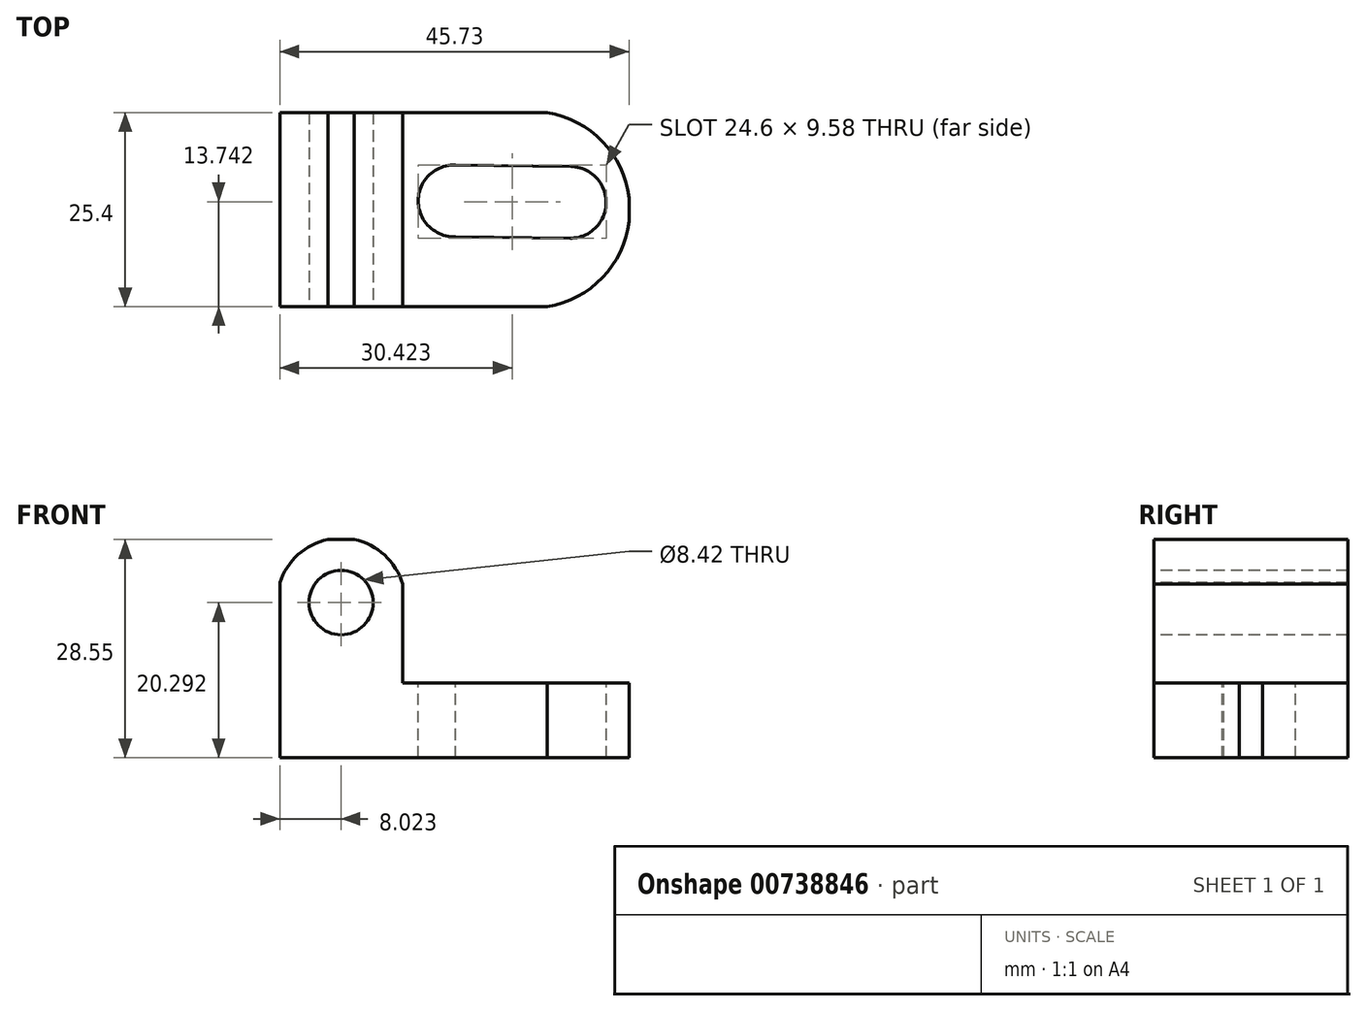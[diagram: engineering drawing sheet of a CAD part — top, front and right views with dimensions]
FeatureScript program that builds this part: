
annotation { "Feature Type Name" : "Feature", "Feature Type Description" : "" }
export const myFeature = defineFeature(function(context is Context, id is Id, definition is map)
    precondition{}
    {
        {
            var Q0;
            Q0=qCreatedBy(makeId("Front.planeOp"),FACE);
            var sketch = newSketch(context, id + "F0", { "sketchPlane" : qUnion([Q0])});
            skLineSegment(sketch, "E0", {"start": v(0, 0) * mm, "end": v(45.73, 0) * mm});
            skLineSegment(sketch, "E1", {"start": v(45.73, 0) * mm, "end": v(45.73, 9.78) * mm});
            skLineSegment(sketch, "E2", {"start": v(45.73, 9.78) * mm, "end": v(16.1, 9.78) * mm});
            skLineSegment(sketch, "E3", {"start": v(16.1, 9.78) * mm, "end": v(16.1, 28.55) * mm});
            skLineSegment(sketch, "E4", {"start": v(16.1, 28.55) * mm, "end": v(0, 28.55) * mm});
            skLineSegment(sketch, "E5", {"start": v(0, 28.55) * mm, "end": v(0, 0) * mm});
            skSolve(sketch);
        }
        {
            var Q0;
            Q0=makeQuery(id+"F0.imprint","IMPRINT",FACE,{"disambiguationData":[TD([[makeQuery(id+"F0.imprint","IMPRINT",EDGE,{"derivedFrom":sQuery(id+"F0.wireOp",EDGE,"E0")}),1.0]])]});
            extrude(context, id + "F1", {"entities" : qUnion([Q0]), "depth" : 25.4 * mm, "offsetDistance" : 25.4 * mm});
        }
        {
            var Q0;
            Q0=makeQuery(id+"F1.opExtrude","SWEPT_FACE",FACE,{"disambiguationData":[OSD([sQuery(id+"F0.wireOp",EDGE,"E2")])]});
            var sketch = newSketch(context, id + "F2", { "sketchPlane" : qUnion([Q0])});
            skCircle(sketch, "E6", {"center": v(22.82, -11.56) * mm, "radius": 4.7 * mm});
            skCircle(sketch, "E7", {"center": v(38.03, -11.75) * mm, "radius": 4.7 * mm});
            skLineSegment(sketch, "E8", {"start": v(23.01, -6.87) * mm, "end": v(38.09, -7.06) * mm});
            skLineSegment(sketch, "E9", {"start": v(23.01, -16.25) * mm, "end": v(38.03, -16.45) * mm});
            skSolve(sketch);
        }
        {
            var Q0;
            {var subQ0=sQuery(id+"F2.wireOp",EDGE,"E6");var subQ1=makeQuery(id+"F2.imprint","INTERSECT",VERTEX,{"derivedFrom":[subQ0,sQuery(id+"F2.wireOp",EDGE,"E8")]});Q0=makeQuery(id+"F2.imprint","IMPRINT",FACE,{"disambiguationData":[TD([[makeQuery(id+"F2.imprint","IMPRINT",EDGE,{"disambiguationData":[TD([[subQ1,-1.0]])],"derivedFrom":subQ0}),1.0]])]});}
            var Q1;
            {var subQ0=sQuery(id+"F2.wireOp",EDGE,"E8");Q1=makeQuery(id+"F2.imprint","IMPRINT",FACE,{"disambiguationData":[TD([[makeQuery(id+"F2.imprint","IMPRINT",EDGE,{"derivedFrom":subQ0}),-1.0]])]});}
            var Q2;
            {var subQ0=sQuery(id+"F2.wireOp",EDGE,"E7");var subQ1=makeQuery(id+"F2.imprint","INTERSECT",VERTEX,{"derivedFrom":[subQ0,sQuery(id+"F2.wireOp",EDGE,"E8")]});Q2=makeQuery(id+"F2.imprint","IMPRINT",FACE,{"disambiguationData":[TD([[makeQuery(id+"F2.imprint","IMPRINT",EDGE,{"disambiguationData":[TD([[subQ1,-1.0]])],"derivedFrom":subQ0}),1.0]])]});}
            extrude(context, id + "F3", {"entities" : qUnion([Q0, Q1, Q2]), "operationType" : NewBodyOperationType.REMOVE, "endBound" : BoundingType.THROUGH_ALL, "oppositeDirection" : true, "depth" : 25.4 * mm, "offsetDistance" : 25.4 * mm});
        }
        {
            var Q0;
            Q0=makeQuery(id+"F1.opExtrude","SWEPT_FACE",FACE,{"disambiguationData":[OSD([sQuery(id+"F0.wireOp",EDGE,"E2")])]});
            var sketch = newSketch(context, id + "F4", { "sketchPlane" : qUnion([Q0])});
            skArc(sketch, "E10", {"start": v(30.92, -25.4) * mm, "mid": v(45.82, -12.7) * mm, "end": v(30.92, 0) * mm});
            skSolve(sketch);
        }
        {
            var Q0;
            {var subQ0=sQuery(id+"F4.wireOp",EDGE,"E10");var subQ1=sQuery(id+"F0.wireOp",EDGE,"E2");var subQ4=makeQuery(id+"F1.opExtrude","CAP_EDGE",EDGE,{"disambiguationData":[OSD([subQ1])],"isStart":true});var subQ5=makeQuery(id+"F4.imprint","INTERSECT",VERTEX,{"disambiguationData":[OD(1.0)],"derivedFrom":[subQ4,subQ0]});Q0=makeQuery(id+"F4.imprint","IMPRINT",FACE,{"disambiguationData":[TD([[makeQuery(id+"F4.imprint","IMPRINT",EDGE,{"disambiguationData":[TD([[subQ5,1.0]])],"derivedFrom":subQ0}),-1.0]])]});}
            var Q1;
            {var subQ0=sQuery(id+"F4.wireOp",EDGE,"E10");var subQ1=sQuery(id+"F0.wireOp",EDGE,"E2");var subQ2=makeQuery(id+"F1.opExtrude","CAP_EDGE",EDGE,{"disambiguationData":[OSD([subQ1])],"isStart":false});var subQ3=makeQuery(id+"F4.imprint","INTERSECT",VERTEX,{"disambiguationData":[OD(1.0)],"derivedFrom":[subQ2,subQ0]});Q1=makeQuery(id+"F4.imprint","IMPRINT",FACE,{"disambiguationData":[TD([[makeQuery(id+"F4.imprint","IMPRINT",EDGE,{"disambiguationData":[TD([[subQ3,-1.0]])],"derivedFrom":subQ0}),-1.0]])]});}
            extrude(context, id + "F5", {"entities" : qUnion([Q0, Q1]), "operationType" : NewBodyOperationType.REMOVE, "endBound" : BoundingType.THROUGH_ALL, "oppositeDirection" : true, "depth" : 25.4 * mm, "offsetDistance" : 25.4 * mm});
        }
        {
            var Q0;
            Q0=makeQuery(id+"F1.opExtrude","CAP_FACE",FACE,{"disambiguationData":[OSD([sQuery(id+"F0.wireOp",EDGE,"E0"),sQuery(id+"F0.wireOp",EDGE,"E1"),sQuery(id+"F0.wireOp",EDGE,"E2"),sQuery(id+"F0.wireOp",EDGE,"E3"),sQuery(id+"F0.wireOp",EDGE,"E4"),sQuery(id+"F0.wireOp",EDGE,"E5")])],"isStart":false});
            var sketch = newSketch(context, id + "F6", { "sketchPlane" : qUnion([Q0])});
            skArc(sketch, "E11", {"start": v(16.1, 17.87) * mm, "mid": v(7.93, 28.72) * mm, "end": v(0, 17.7) * mm});
            skSolve(sketch);
        }
        {
            var Q0;
            {var subQ0=sQuery(id+"F6.wireOp",EDGE,"E11");var subQ1=makeQuery(id+"F1.opExtrude","CAP_EDGE",EDGE,{"disambiguationData":[OSD([sQuery(id+"F0.wireOp",EDGE,"E4")])],"isStart":false});var subQ2=makeQuery(id+"F6.imprint","INTERSECT",VERTEX,{"disambiguationData":[OD(1.0)],"derivedFrom":[subQ1,subQ0]});Q0=makeQuery(id+"F6.imprint","IMPRINT",FACE,{"disambiguationData":[TD([[makeQuery(id+"F6.imprint","IMPRINT",EDGE,{"disambiguationData":[TD([[subQ2,-1.0]])],"derivedFrom":subQ0}),-1.0]])]});}
            var Q1;
            {var subQ0=sQuery(id+"F6.wireOp",EDGE,"E11");var subQ1=makeQuery(id+"F1.opExtrude","CAP_EDGE",EDGE,{"disambiguationData":[OSD([sQuery(id+"F0.wireOp",EDGE,"E3")])],"isStart":false});var subQ2=makeQuery(id+"F6.imprint","INTERSECT",VERTEX,{"disambiguationData":[OD(1.0)],"derivedFrom":[subQ1,subQ0]});Q1=makeQuery(id+"F6.imprint","IMPRINT",FACE,{"disambiguationData":[TD([[makeQuery(id+"F6.imprint","IMPRINT",EDGE,{"disambiguationData":[TD([[subQ2,-1.0]])],"derivedFrom":subQ0}),-1.0]])]});}
            extrude(context, id + "F7", {"entities" : qUnion([Q0, Q1]), "operationType" : NewBodyOperationType.REMOVE, "endBound" : BoundingType.THROUGH_ALL, "oppositeDirection" : true, "depth" : 25.4 * mm, "offsetDistance" : 25.4 * mm});
        }
        {
            var Q0;
            Q0=makeQuery(id+"F1.opExtrude","CAP_FACE",FACE,{"disambiguationData":[OSD([sQuery(id+"F0.wireOp",EDGE,"E0"),sQuery(id+"F0.wireOp",EDGE,"E1"),sQuery(id+"F0.wireOp",EDGE,"E2"),sQuery(id+"F0.wireOp",EDGE,"E3"),sQuery(id+"F0.wireOp",EDGE,"E4"),sQuery(id+"F0.wireOp",EDGE,"E5")])],"isStart":false});
            var sketch = newSketch(context, id + "F8", { "sketchPlane" : qUnion([Q0])});
            skCircle(sketch, "E12", {"center": v(8.02, 20.3) * mm, "radius": 4.2 * mm});
            skSolve(sketch);
        }
        {
            var Q0;
            Q0=makeQuery(id+"F8.imprint","IMPRINT",FACE,{"disambiguationData":[TD([[makeQuery(id+"F8.imprint","IMPRINT",EDGE,{"derivedFrom":sQuery(id+"F8.wireOp",EDGE,"E12")}),1.0]])]});
            extrude(context, id + "F9", {"entities" : qUnion([Q0]), "operationType" : NewBodyOperationType.REMOVE, "endBound" : BoundingType.THROUGH_ALL, "oppositeDirection" : true, "depth" : 25.4 * mm, "offsetDistance" : 25.4 * mm});
        }
    });
